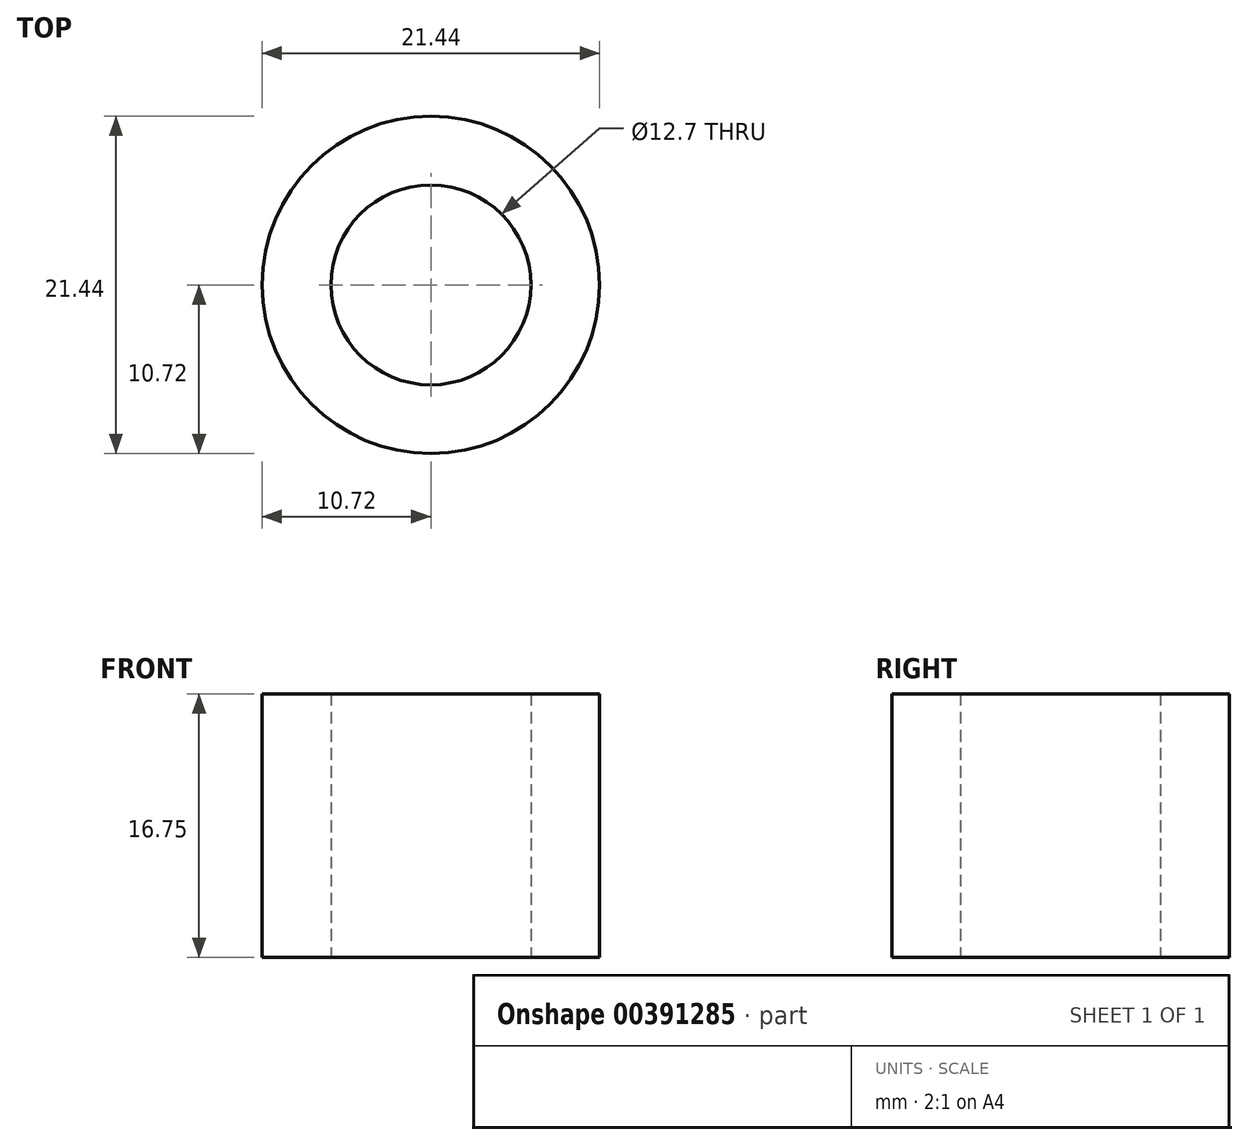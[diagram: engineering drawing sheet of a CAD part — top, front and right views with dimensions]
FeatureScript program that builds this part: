
annotation { "Feature Type Name" : "Feature", "Feature Type Description" : "" }
export const myFeature = defineFeature(function(context is Context, id is Id, definition is map)
    precondition{}
    {
        {
            assignVariable(context, id + "F0", {"name" : "Length", "anyValue" : 16.75});
        }
        {
            var Q0;
            Q0=qCreatedBy(makeId("Top.planeOp"),FACE);
            var sketch = newSketch(context, id + "F1", { "sketchPlane" : qUnion([Q0])});
            skCircle(sketch, "E0", {"center": v(0, 0) * mm, "radius": 10.72 * mm});
            skCircle(sketch, "E1", {"center": v(0, 0) * mm, "radius": 6.35 * mm});
            skSolve(sketch);
        }
        {
            var Q0;
            Q0=makeQuery(id+"F1.imprint","IMPRINT",FACE,{"disambiguationData":[TD([[makeQuery(id+"F1.imprint","IMPRINT",EDGE,{"derivedFrom":sQuery(id+"F1.wireOp",EDGE,"E0")}),1.0]])]});
            extrude(context, id + "F2", {"entities" : qUnion([Q0]), "depth" : (getVariable(context, 'Length')) * mm});
        }
    });
